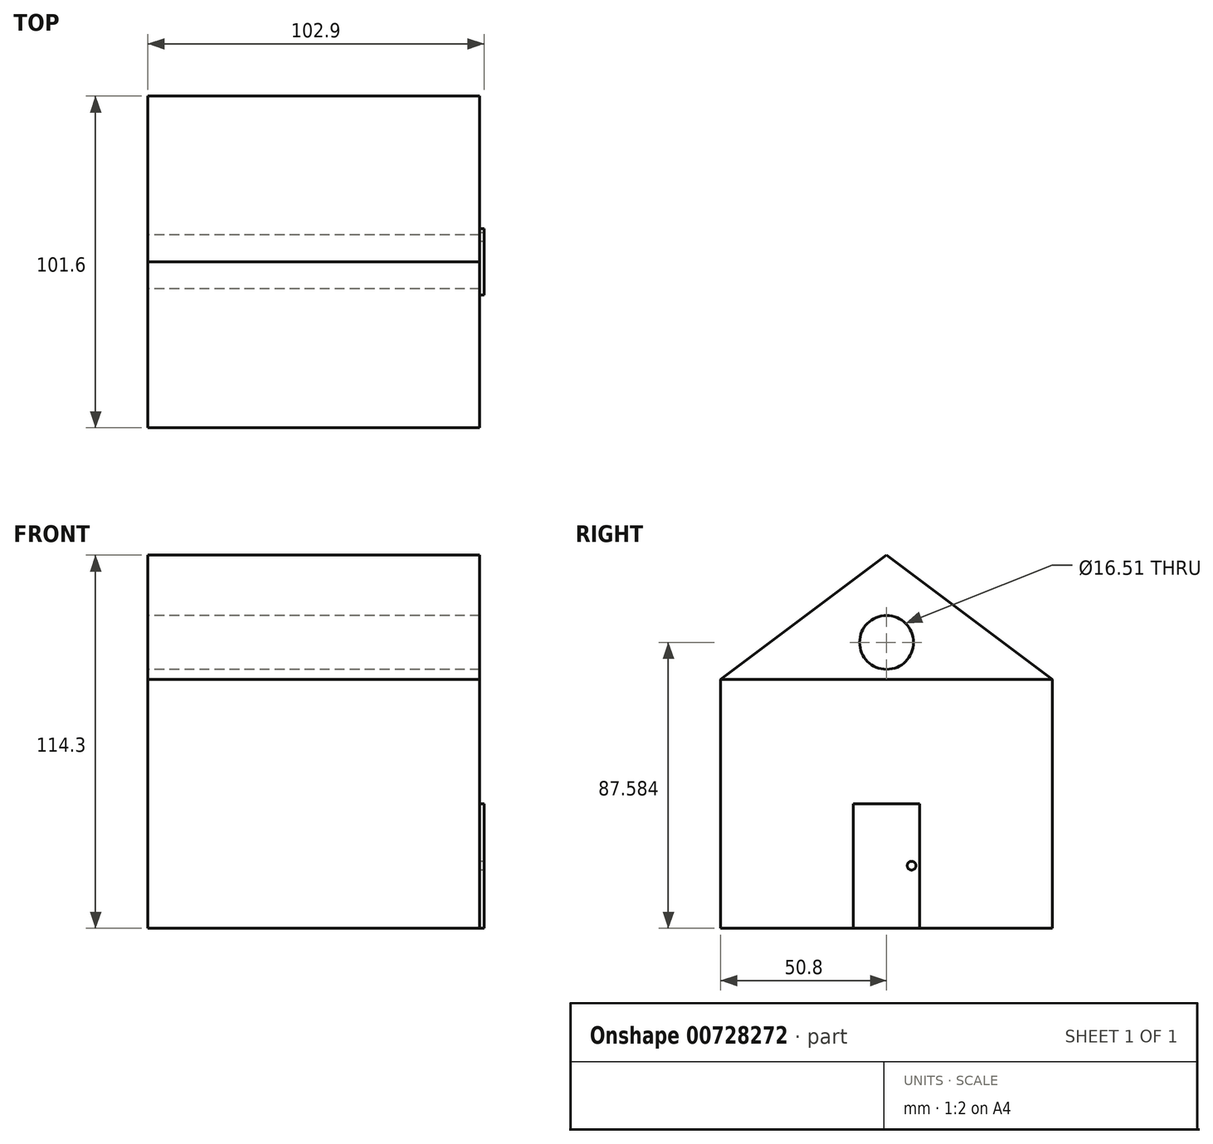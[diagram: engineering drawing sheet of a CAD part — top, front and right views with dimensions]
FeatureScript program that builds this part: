
annotation { "Feature Type Name" : "Feature", "Feature Type Description" : "" }
export const myFeature = defineFeature(function(context is Context, id is Id, definition is map)
    precondition{}
    {
        {
            var Q0;
            Q0=qCreatedBy(makeId("Right.planeOp"),FACE);
            var sketch = newSketch(context, id + "F0", { "sketchPlane" : qUnion([Q0])});
            skLineSegment(sketch, "E0.bottom", {"start": v(50.8, 38.1) * mm, "end": v(-50.8, 38.1) * mm});
            skLineSegment(sketch, "E0.top", {"start": v(50.8, -38.1) * mm, "end": v(-50.8, -38.1) * mm});
            skLineSegment(sketch, "E0.left", {"start": v(50.8, 38.1) * mm, "end": v(50.8, -38.1) * mm});
            skLineSegment(sketch, "E0.right", {"start": v(-50.8, 38.1) * mm, "end": v(-50.8, -38.1) * mm});
            skPoint(sketch, "E0.middle", {"position": v(0, 0) * mm});
            skLineSegment(sketch, "E1", {"start": v(-50.8, 38.1) * mm, "end": v(0, 76.2) * mm});
            skLineSegment(sketch, "E2", {"start": v(0, 76.2) * mm, "end": v(50.8, 38.1) * mm});
            skSolve(sketch);
        }
        {
            var Q0;
            Q0=makeQuery(id+"F0.imprint","IMPRINT",FACE,{"disambiguationData":[TD([[makeQuery(id+"F0.imprint","IMPRINT",EDGE,{"derivedFrom":sQuery(id+"F0.wireOp",EDGE,"E0.bottom")}),-1.0]])]});
            var sketch = newSketch(context, id + "F1", { "sketchPlane" : qUnion([Q0])});
            skCircle(sketch, "E3", {"center": v(0, 49.48) * mm, "radius": 8.26 * mm});
            skLineSegment(sketch, "E4", {"start": v(0, 49.48) * mm, "end": v(-8.26, 49.48) * mm});
            skLineSegment(sketch, "E5", {"start": v(0, 49.48) * mm, "end": v(0, 57.74) * mm});
            skLineSegment(sketch, "E6", {"start": v(0, 57.74) * mm, "end": v(0, 49.48) * mm});
            skLineSegment(sketch, "E7", {"start": v(8.26, 49.48) * mm, "end": v(0, 49.48) * mm});
            skLineSegment(sketch, "E8", {"start": v(0, 41.23) * mm, "end": v(0, 49.48) * mm});
            skLineSegment(sketch, "E9.bottom", {"start": v(-12.7, -38.1) * mm, "end": v(12.7, -38.1) * mm});
            skLineSegment(sketch, "E9.top", {"start": v(-12.7, 0) * mm, "end": v(12.7, 0) * mm});
            skLineSegment(sketch, "E9.left", {"start": v(-12.7, -38.1) * mm, "end": v(-12.7, 0) * mm});
            skLineSegment(sketch, "E9.right", {"start": v(12.7, -38.1) * mm, "end": v(12.7, 0) * mm});
            skCircle(sketch, "E10", {"center": v(6.57, -19.72) * mm, "radius": 2.26 * mm});
            skSolve(sketch);
        }
        {
            var Q0;
            Q0=makeQuery(id+"F0.imprint","IMPRINT",FACE,{"disambiguationData":[TD([[makeQuery(id+"F0.imprint","IMPRINT",EDGE,{"derivedFrom":sQuery(id+"F0.wireOp",EDGE,"E0.bottom")}),1.0]])]});
            var Q1;
            Q1=makeQuery(id+"F1.imprint","IMPRINT",FACE,{"disambiguationData":[TD([[makeQuery(id+"F1.imprint","IMPRINT",EDGE,{"derivedFrom":makeQuery(id+"F0.imprint","IMPRINT",EDGE,{"derivedFrom":sQuery(id+"F0.wireOp",EDGE,"E0.bottom")})}),-1.0]])]});
            extrude(context, id + "F2", {"entities" : qUnion([Q0, Q1]), "depth" : 50.8 * mm, "offsetDistance" : 25.4 * mm, "hasSecondDirection" : true, "secondDirectionOppositeDirection" : true, "secondDirectionDepth" : 50.8 * mm});
        }
        {
            var Q0;
            Q0=makeQuery(id+"F2.opExtrude","CAP_FACE",FACE,{"disambiguationData":[OSD([sQuery(id+"F0.wireOp",EDGE,"E0.bottom"),sQuery(id+"F0.wireOp",EDGE,"E0.top"),sQuery(id+"F0.wireOp",EDGE,"E0.left"),sQuery(id+"F0.wireOp",EDGE,"E0.right")])],"isStart":false});
            var sketch = newSketch(context, id + "F3", { "sketchPlane" : qUnion([Q0])});
            skLineSegment(sketch, "E11.bottom", {"start": v(-10.16, 0) * mm, "end": v(10.16, 0) * mm});
            skLineSegment(sketch, "E11.top", {"start": v(-10.16, -38.1) * mm, "end": v(10.16, -38.1) * mm});
            skLineSegment(sketch, "E11.left", {"start": v(-10.16, 0) * mm, "end": v(-10.16, -38.1) * mm});
            skLineSegment(sketch, "E11.right", {"start": v(10.16, 0) * mm, "end": v(10.16, -38.1) * mm});
            skPoint(sketch, "E11.middle", {"position": v(0, -19.05) * mm});
            skCircle(sketch, "E12", {"center": v(7.65, -18.9) * mm, "radius": 1.33 * mm});
            skSolve(sketch);
        }
        {
            var Q0;
            Q0=makeQuery(id+"F3.imprint","IMPRINT",FACE,{"disambiguationData":[TD([[makeQuery(id+"F3.imprint","IMPRINT",EDGE,{"derivedFrom":sQuery(id+"F3.wireOp",EDGE,"E11.bottom")}),-1.0]])]});
            extrude(context, id + "F4", {"entities" : qUnion([Q0]), "operationType" : NewBodyOperationType.ADD, "depth" : 1.3 * mm, "offsetDistance" : 25.4 * mm});
        }
    });
